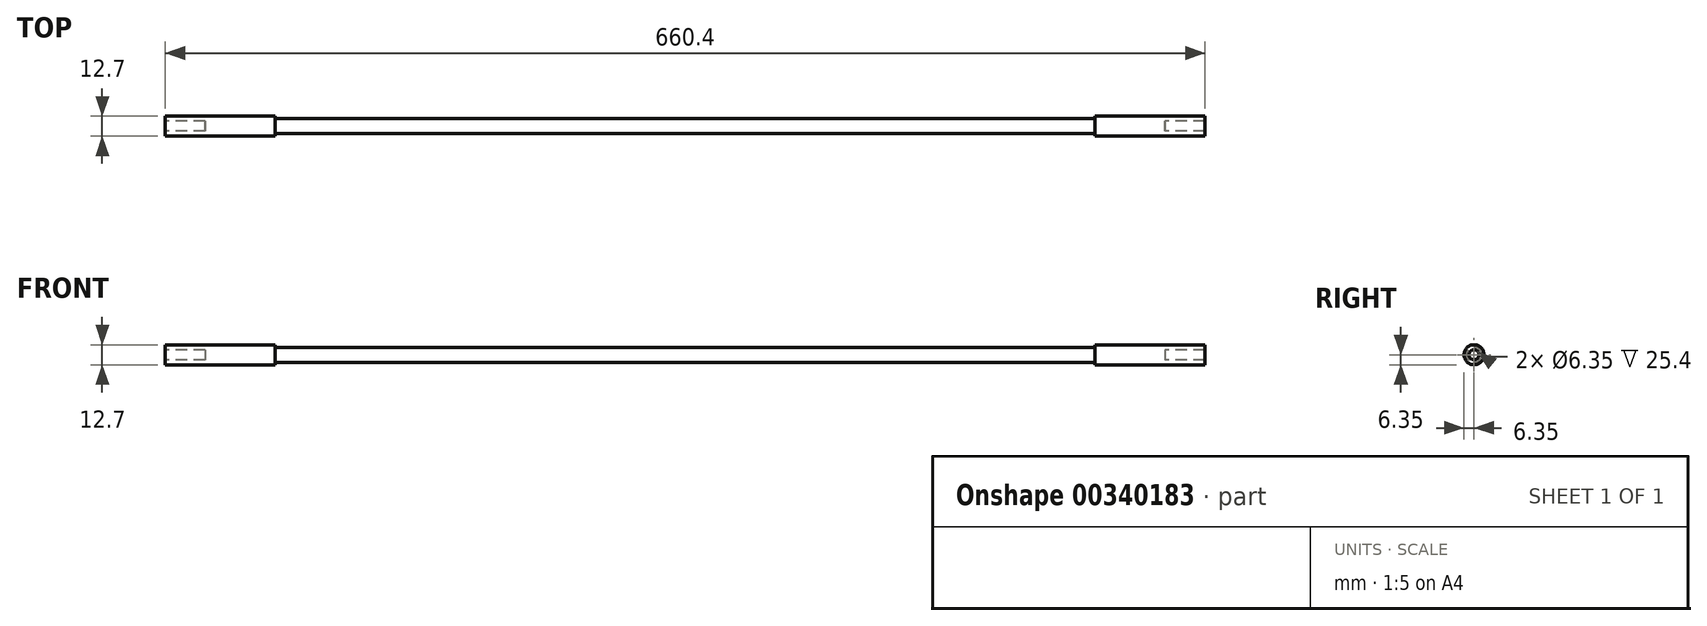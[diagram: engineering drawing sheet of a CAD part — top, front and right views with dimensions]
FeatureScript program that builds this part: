
annotation { "Feature Type Name" : "Feature", "Feature Type Description" : "" }
export const myFeature = defineFeature(function(context is Context, id is Id, definition is map)
    precondition{}
    {
        {
            var Q0;
            Q0=qCreatedBy(makeId("Front.planeOp"),FACE);
            var sketch = newSketch(context, id + "F0", { "sketchPlane" : qUnion([Q0])});
            skLineSegment(sketch, "E0", {"start": v(0, 0) * mm, "end": v(635, 0) * mm});
            skLineSegment(sketch, "E1", {"start": v(25.4, 0) * mm, "end": v(25.4, 3.17) * mm});
            skLineSegment(sketch, "E2", {"start": v(25.4, 3.17) * mm, "end": v(0, 3.17) * mm});
            skLineSegment(sketch, "E3", {"start": v(0, 3.17) * mm, "end": v(0, 6.35) * mm});
            skLineSegment(sketch, "E4", {"start": v(0, 6.35) * mm, "end": v(69.85, 6.35) * mm});
            skLineSegment(sketch, "E5", {"start": v(69.85, 6.35) * mm, "end": v(69.85, 4.76) * mm});
            skLineSegment(sketch, "E6", {"start": v(69.85, 4.76) * mm, "end": v(590.55, 4.76) * mm});
            skLineSegment(sketch, "E7", {"start": v(590.55, 4.76) * mm, "end": v(590.55, 6.35) * mm});
            skLineSegment(sketch, "E8", {"start": v(590.55, 6.35) * mm, "end": v(660.4, 6.35) * mm});
            skLineSegment(sketch, "E9", {"start": v(660.4, 6.35) * mm, "end": v(660.4, 3.18) * mm});
            skLineSegment(sketch, "E10", {"start": v(660.4, 3.18) * mm, "end": v(635, 3.18) * mm});
            skLineSegment(sketch, "E11", {"start": v(635, 3.18) * mm, "end": v(635, 0) * mm});
            skSolve(sketch);
        }
        {
            var Q0;
            Q0 = qSketchRegion(id + "F0", true);
            var Q1;
            Q1=sQuery(id+"F0.wireOp",EDGE,"E0");
            revolve(context, id + "F1", {"entities" : qUnion([Q0]), "axis" : qUnion([Q1]), "revolveType" : RevolveType.FULL});
        }
    });
